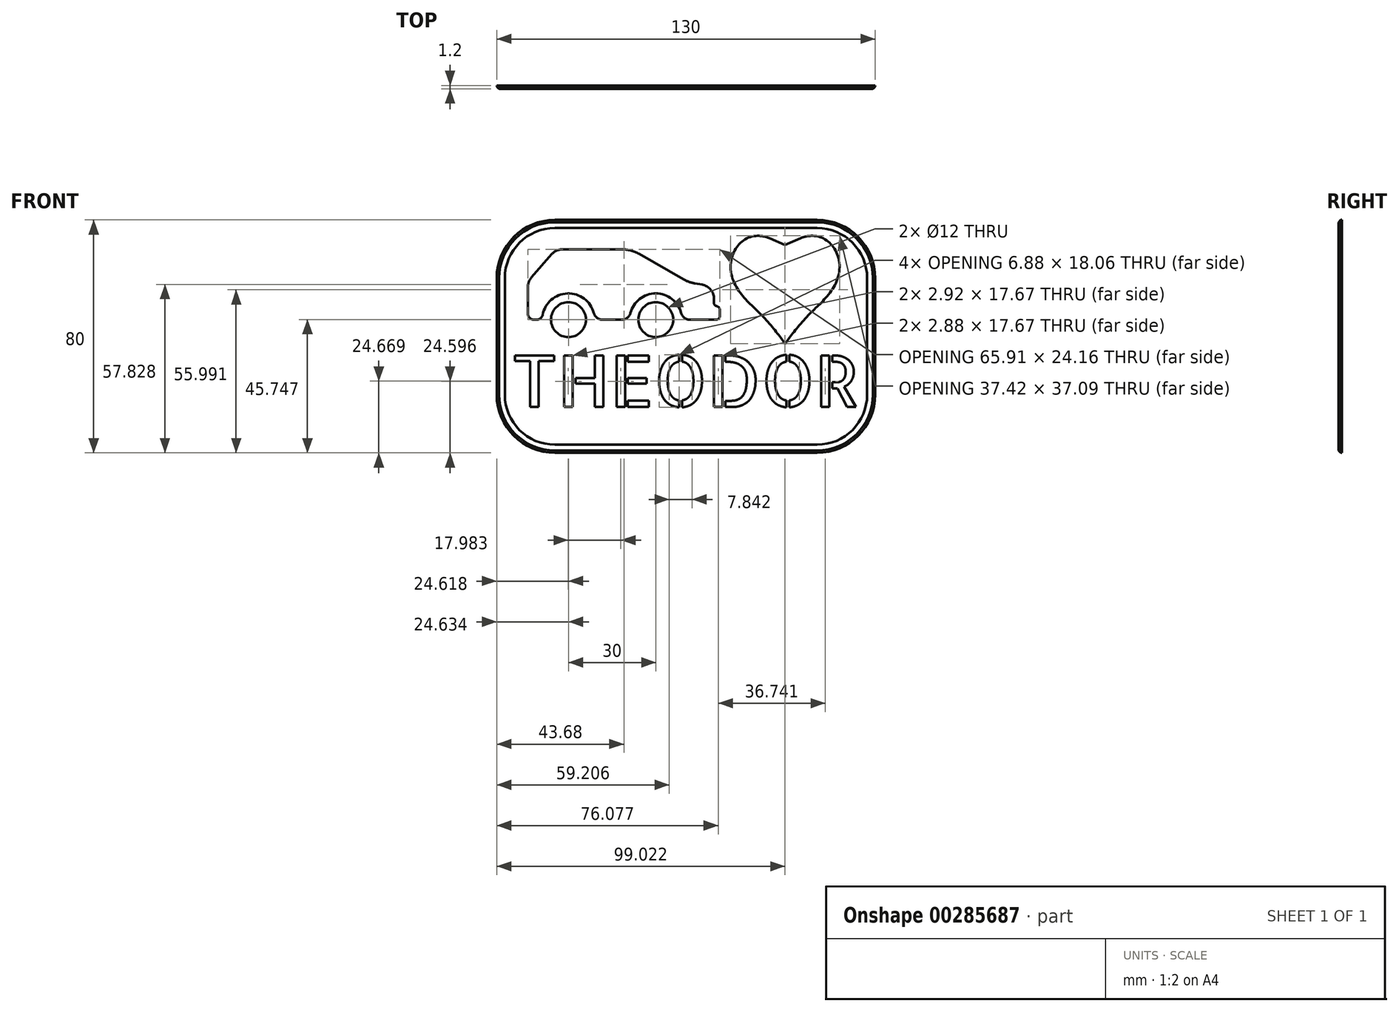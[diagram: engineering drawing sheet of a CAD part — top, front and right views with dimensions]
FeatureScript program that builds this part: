
annotation { "Feature Type Name" : "Feature", "Feature Type Description" : "" }
export const myFeature = defineFeature(function(context is Context, id is Id, definition is map)
    precondition{}
    {
        {
            var Q0;
            Q0=qCreatedBy(makeId("Front.planeOp"),FACE);
            var sketch = newSketch(context, id + "F0", { "sketchPlane" : qUnion([Q0])});
            skLineSegment(sketch, "E0.bottom", {"start": v(-65, 60) * mm, "end": v(65, 60) * mm});
            skLineSegment(sketch, "E0.top", {"start": v(-65, -20) * mm, "end": v(65, -20) * mm});
            skLineSegment(sketch, "E0.left", {"start": v(-65, 60) * mm, "end": v(-65, -20) * mm});
            skLineSegment(sketch, "E0.right", {"start": v(65, 60) * mm, "end": v(65, -20) * mm});
            skSolve(sketch);
        }
        {
            var Q0;
            Q0=qSketchRegion(id+"F0",true);
            extrude(context, id + "F1", {"entities" : qUnion([Q0]), "depth" : 1.2 * mm});
        }
        {
            var Q0;
            Q0=makeQuery(id+"F1.opExtrude","CAP_FACE",FACE,{"disambiguationData":[OSD([sQuery(id+"F0.wireOp",EDGE,"E0.bottom"),sQuery(id+"F0.wireOp",EDGE,"E0.top"),sQuery(id+"F0.wireOp",EDGE,"E0.left"),sQuery(id+"F0.wireOp",EDGE,"E0.right")])],"isStart":false});
            var sketch = newSketch(context, id + "F2", { "sketchPlane" : qUnion([Q0])});
            skText(sketch, "E1", { "text": "THEODOR", "fontName": "AllertaStencil-Regular.ttf"});
            skText(sketch, "E2", { "text": "♥", "fontName": "NotoSansCJKjp-Regular.otf"});
            const initialGuessF2  = {"E1": [-0.06, -0.00424, 1, 0, 0.01768], "E2": [0.0118, 0.01916, 1, 0, 0.032]};
            skSetInitialGuess(sketch, initialGuessF2);
            skSolve(sketch);
        }
        {
            var Q0;
            Q0=qSketchRegion(id+"F2",true);
            extrude(context, id + "F3", {"entities" : qUnion([Q0]), "operationType" : NewBodyOperationType.REMOVE, "endBound" : BoundingType.THROUGH_ALL, "oppositeDirection" : true, "depth" : 25 * mm});
        }
        {
            var Q0;
            Q0=makeQuery(id+"F1.opExtrude","SWEPT_EDGE",EDGE,{"disambiguationData":[OSD([sQuery(id+"F0.wireOp",EDGE,"E0.top"),sQuery(id+"F0.wireOp",EDGE,"E0.right")])]});
            var Q1;
            Q1=makeQuery(id+"F1.opExtrude","SWEPT_EDGE",EDGE,{"disambiguationData":[OSD([sQuery(id+"F0.wireOp",EDGE,"E0.bottom"),sQuery(id+"F0.wireOp",EDGE,"E0.right")])]});
            var Q2;
            Q2=makeQuery(id+"F1.opExtrude","SWEPT_EDGE",EDGE,{"disambiguationData":[OSD([sQuery(id+"F0.wireOp",EDGE,"E0.top"),sQuery(id+"F0.wireOp",EDGE,"E0.left")])]});
            var Q3;
            Q3=makeQuery(id+"F1.opExtrude","SWEPT_EDGE",EDGE,{"disambiguationData":[OSD([sQuery(id+"F0.wireOp",EDGE,"E0.bottom"),sQuery(id+"F0.wireOp",EDGE,"E0.left")])]});
            fillet(context, id + "F4", {"entities" : qUnion([Q0, Q1, Q2, Q3]), "radius" : 20 * mm, "tangentPropagation" : true, "allowEdgeOverflow" : false});
        }
        {
            var Q0;
            Q0=makeQuery(id+"F1.opExtrude","CAP_EDGE",EDGE,{"disambiguationData":[OSD([sQuery(id+"F0.wireOp",EDGE,"E0.top")])],"isStart":false});
            chamfer(context, id + "F5", {"entities" : qUnion([Q0]), "width" : 0.8 * mm, "tangentPropagation" : true});
        }
        {
            var Q0;
            Q0=makeQuery(id+"F1.opExtrude","CAP_FACE",FACE,{"disambiguationData":[OSD([sQuery(id+"F0.wireOp",EDGE,"E0.bottom"),sQuery(id+"F0.wireOp",EDGE,"E0.top"),sQuery(id+"F0.wireOp",EDGE,"E0.left"),sQuery(id+"F0.wireOp",EDGE,"E0.right")])],"isStart":false});
            var sketch = newSketch(context, id + "F6", { "sketchPlane" : qUnion([Q0])});
            skLineSegment(sketch, "E3.0", {"start": v(45, 57.2) * mm, "end": v(-45, 57.2) * mm});
            skArc(sketch, "E3.1", {"start": v(62.2, 40) * mm, "mid": v(57.16, 52.16) * mm, "end": v(45, 57.2) * mm});
            skArc(sketch, "E3.2", {"start": v(-45, 57.2) * mm, "mid": v(-57.16, 52.16) * mm, "end": v(-62.2, 40) * mm});
            skLineSegment(sketch, "E3.3", {"start": v(62.2, 0) * mm, "end": v(62.2, 40) * mm});
            skLineSegment(sketch, "E3.4", {"start": v(-62.2, 40) * mm, "end": v(-62.2, 0) * mm});
            skArc(sketch, "E3.5", {"start": v(-62.2, 0) * mm, "mid": v(-57.16, -12.16) * mm, "end": v(-45, -17.2) * mm});
            skLineSegment(sketch, "E3.6", {"start": v(-45, -17.2) * mm, "end": v(45, -17.2) * mm});
            skArc(sketch, "E3.7", {"start": v(45, -17.2) * mm, "mid": v(57.16, -12.16) * mm, "end": v(62.2, 0) * mm});
            skSolve(sketch);
        }
        {
            var Q0;
            Q0 = qSketchRegion(id + "F6", true);
            extrude(context, id + "F7", {"entities" : qUnion([Q0]), "operationType" : NewBodyOperationType.REMOVE, "oppositeDirection" : true, "depth" : 0.4 * mm});
        }
        {
            var Q0;
            Q0=makeQuery(id+"F7.boolean.opBoolean","COPY",FACE,{"derivedFrom":makeQuery(id+"F7.opExtrude","CAP_FACE",FACE,{"disambiguationData":[OSD([sQuery(id+"F6.wireOp",EDGE,"E3.0"),sQuery(id+"F6.wireOp",EDGE,"E3.1"),sQuery(id+"F6.wireOp",EDGE,"E3.2"),sQuery(id+"F6.wireOp",EDGE,"E3.3"),sQuery(id+"F6.wireOp",EDGE,"E3.4"),sQuery(id+"F6.wireOp",EDGE,"E3.5"),sQuery(id+"F6.wireOp",EDGE,"E3.6"),sQuery(id+"F6.wireOp",EDGE,"E3.7")])],"isStart":false})});
            var sketch = newSketch(context, id + "F8", { "sketchPlane" : qUnion([Q0])});
            skLineSegment(sketch, "E4", {"start": v(39.43, 53.76) * mm, "end": v(33.98, 51.46) * mm});
            skLineSegment(sketch, "E5", {"start": v(33.98, 51.46) * mm, "end": v(28.64, 53.75) * mm});
            skLineSegment(sketch, "E6", {"start": v(28.64, 53.75) * mm, "end": v(28.64, 44.97) * mm});
            skLineSegment(sketch, "E7", {"start": v(28.64, 44.97) * mm, "end": v(40.8, 44.97) * mm});
            skLineSegment(sketch, "E8", {"start": v(40.8, 44.97) * mm, "end": v(39.43, 53.76) * mm});
            skSolve(sketch);
        }
        {
            var Q0;
            Q0 = qSketchRegion(id + "F8", true);
            extrude(context, id + "F9", {"entities" : qUnion([Q0]), "operationType" : NewBodyOperationType.REMOVE, "oppositeDirection" : true, "depth" : 25 * mm});
        }
        {
            var Q0;
            Q0=qCreatedBy(makeId("Front.planeOp"),FACE);
            var sketch = newSketch(context, id + "F10", { "sketchPlane" : qUnion([Q0])});
            skLineSegment(sketch, "E9", {"start": v(-28.75, 25.75) * mm, "end": v(-21.99, 25.75) * mm, "construction": true});
            skCircle(sketch, "E10", {"center": v(-40.37, 25.75) * mm, "radius": 6 * mm});
            skCircle(sketch, "E11", {"center": v(-10.37, 25.75) * mm, "radius": 6 * mm});
            skArc(sketch, "E12", {"start": v(-31.65, 28) * mm, "mid": v(-40.68, 34.74) * mm, "end": v(-49.22, 27.38) * mm});
            skArc(sketch, "E13", {"start": v(-1.65, 28) * mm, "mid": v(-10.37, 34.75) * mm, "end": v(-19.08, 28) * mm});
            skLineSegment(sketch, "E14", {"start": v(-20.37, 25.75) * mm, "end": v(-30.37, 25.75) * mm});
            skLineSegment(sketch, "E15", {"start": v(-51.18, 25.75) * mm, "end": v(-52.27, 25.75) * mm});
            skLineSegment(sketch, "E16", {"start": v(-54.27, 27.75) * mm, "end": v(-54.27, 37.02) * mm});
            skLineSegment(sketch, "E17", {"start": v(-53.03, 40.32) * mm, "end": v(-46.1, 48.2) * mm});
            skLineSegment(sketch, "E18", {"start": v(-42.35, 49.9) * mm, "end": v(-22.06, 49.9) * mm});
            skLineSegment(sketch, "E19", {"start": v(-16.1, 48.33) * mm, "end": v(-0.8, 39.58) * mm});
            skLineSegment(sketch, "E20", {"start": v(3.09, 38.18) * mm, "end": v(5.5, 37.76) * mm});
            skLineSegment(sketch, "E21", {"start": v(9.63, 32.84) * mm, "end": v(9.63, 31.4) * mm});
            skLineSegment(sketch, "E22", {"start": v(10.31, 30.4) * mm, "end": v(10.63, 30.4) * mm});
            skLineSegment(sketch, "E23", {"start": v(11.63, 29.09) * mm, "end": v(11.63, 27.07) * mm});
            skLineSegment(sketch, "E24", {"start": v(10.31, 25.75) * mm, "end": v(1.25, 25.75) * mm});
            skPoint(sketch, "E25.visualSharp", {"position": v(-54.27, 38.9) * mm});
            skArc(sketch, "E25.filletArc", {"start": v(-53.03, 40.32) * mm, "mid": v(-53.95, 38.78) * mm, "end": v(-54.27, 37.02) * mm});
            skPoint(sketch, "E26.visualSharp", {"position": v(-44.6, 49.9) * mm});
            skArc(sketch, "E26.filletArc", {"start": v(-42.35, 49.9) * mm, "mid": v(-44.4, 49.46) * mm, "end": v(-46.1, 48.2) * mm});
            skPoint(sketch, "E27.visualSharp", {"position": v(-18.88, 49.9) * mm});
            skArc(sketch, "E27.filletArc", {"start": v(-16.1, 48.33) * mm, "mid": v(-18.98, 49.5) * mm, "end": v(-22.06, 49.9) * mm});
            skPoint(sketch, "E28.visualSharp", {"position": v(1.02, 38.54) * mm});
            skArc(sketch, "E28.filletArc", {"start": v(-0.8, 39.58) * mm, "mid": v(1.08, 38.71) * mm, "end": v(3.09, 38.18) * mm});
            skPoint(sketch, "E29.visualSharp", {"position": v(9.63, 37.04) * mm});
            skArc(sketch, "E29.filletArc", {"start": v(9.63, 32.84) * mm, "mid": v(8.46, 36.06) * mm, "end": v(5.5, 37.76) * mm});
            skPoint(sketch, "E30.visualSharp", {"position": v(11.63, 30.4) * mm});
            skArc(sketch, "E30.filletArc", {"start": v(11.63, 29.09) * mm, "mid": v(11.25, 30.02) * mm, "end": v(10.31, 30.4) * mm});
            skPoint(sketch, "E31.visualSharp", {"position": v(11.63, 25.75) * mm});
            skArc(sketch, "E31.filletArc", {"start": v(10.31, 25.75) * mm, "mid": v(11.25, 26.13) * mm, "end": v(11.63, 27.07) * mm});
            skPoint(sketch, "E32.visualSharp", {"position": v(9.63, 30.4) * mm});
            skArc(sketch, "E32.filletArc", {"start": v(9.63, 31.4) * mm, "mid": v(9.93, 30.7) * mm, "end": v(10.63, 30.4) * mm});
            skPoint(sketch, "E33.newPointA", {"position": v(-31.37, 25.75) * mm});
            skPoint(sketch, "E33.newPointB", {"position": v(-49.41, 25.75) * mm});
            skArc(sketch, "E33.filletArc", {"start": v(-31.65, 28) * mm, "mid": v(-30.58, 26.38) * mm, "end": v(-28.75, 25.75) * mm});
            skArc(sketch, "E34.filletArc", {"start": v(-21.99, 25.75) * mm, "mid": v(-20.15, 26.38) * mm, "end": v(-19.08, 28) * mm});
            skPoint(sketch, "E35.visualSharp", {"position": v(-1.37, 25.75) * mm});
            skArc(sketch, "E35.filletArc", {"start": v(-1.65, 28) * mm, "mid": v(-0.58, 26.38) * mm, "end": v(1.25, 25.75) * mm});
            skPoint(sketch, "E36.visualSharp", {"position": v(-49.37, 25.75) * mm});
            skArc(sketch, "E36.filletArc", {"start": v(-51.18, 25.75) * mm, "mid": v(-49.9, 26.2) * mm, "end": v(-49.22, 27.38) * mm});
            skPoint(sketch, "E37.visualSharp", {"position": v(-54.27, 25.75) * mm});
            skArc(sketch, "E37.filletArc", {"start": v(-54.27, 27.75) * mm, "mid": v(-53.69, 26.33) * mm, "end": v(-52.27, 25.75) * mm});
            skSolve(sketch);
        }
        {
            var Q0;
            Q0 = qSketchRegion(id + "F10", true);
            extrude(context, id + "F11", {"entities" : qUnion([Q0]), "operationType" : NewBodyOperationType.REMOVE, "depth" : 25 * mm});
        }
    });
